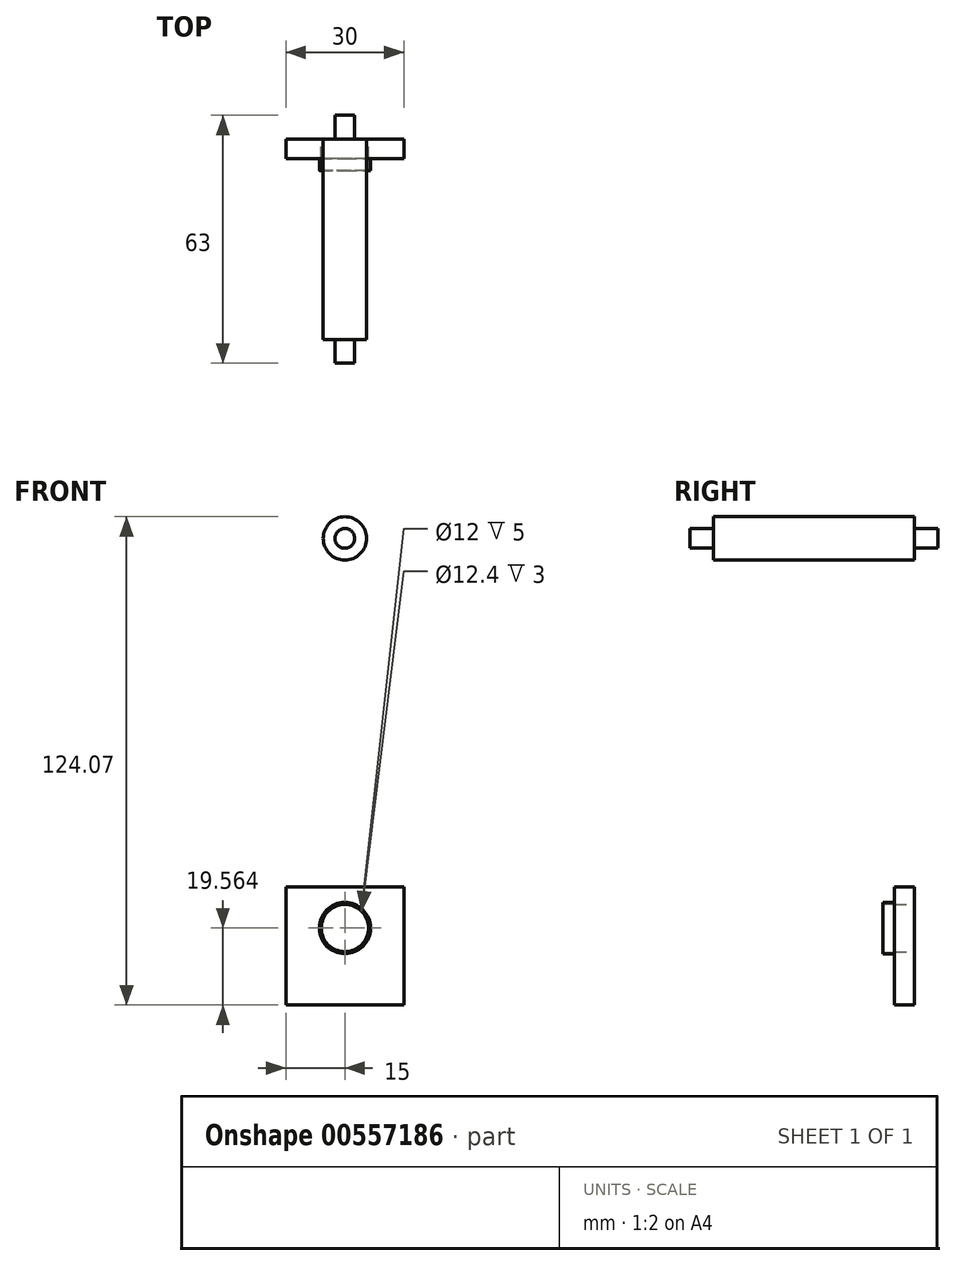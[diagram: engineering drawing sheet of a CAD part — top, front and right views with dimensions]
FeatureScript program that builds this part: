
annotation { "Feature Type Name" : "Feature", "Feature Type Description" : "" }
export const myFeature = defineFeature(function(context is Context, id is Id, definition is map)
    precondition{}
    {
        {
            var Q0;
            Q0=qCreatedBy(makeId("Front.planeOp"),FACE);
            var sketch = newSketch(context, id + "F0", { "sketchPlane" : qUnion([Q0])});
            skCircle(sketch, "E0", {"center": v(0, 0) * mm, "radius": 6 * mm});
            skCircle(sketch, "E1", {"center": v(0, 0) * mm, "radius": 5.7 * mm});
            skSolve(sketch);
        }
        {
            var Q0;
            Q0=makeQuery(id+"F0.imprint","IMPRINT",FACE,{"disambiguationData":[TD([[makeQuery(id+"F0.imprint","IMPRINT",EDGE,{"derivedFrom":sQuery(id+"F0.wireOp",EDGE,"E0")}),1.0]])]});
            extrude(context, id + "F1", {"entities" : qUnion([Q0]), "depth" : 50 * mm, "offsetDistance" : 25 * mm});
        }
        {
            var Q0;
            Q0=qCreatedBy(makeId("Front.planeOp"),FACE);
            var sketch = newSketch(context, id + "F2", { "sketchPlane" : qUnion([Q0])});
            skCircle(sketch, "E2", {"center": v(0, 53.13) * mm, "radius": 5.5 * mm});
            skSolve(sketch);
        }
        {
            var Q0;
            Q0=makeQuery(id+"F2.imprint","IMPRINT",FACE,{"disambiguationData":[TD([[makeQuery(id+"F2.imprint","IMPRINT",EDGE,{"derivedFrom":sQuery(id+"F2.wireOp",EDGE,"E2")}),1.0]])]});
            extrude(context, id + "F3", {"entities" : qUnion([Q0]), "depth" : 51 * mm, "offsetDistance" : 25 * mm});
        }
        {
            var Q0;
            Q0=qCreatedBy(makeId("Front.planeOp"),FACE);
            var sketch = newSketch(context, id + "F4", { "sketchPlane" : qUnion([Q0])});
            skCircle(sketch, "E3", {"center": v(0, 21.61) * mm, "radius": 8.5 * mm});
            skSolve(sketch);
        }
        {
            var Q0;
            Q0=makeQuery(id+"F4.imprint","IMPRINT",FACE,{"disambiguationData":[TD([[makeQuery(id+"F4.imprint","IMPRINT",EDGE,{"derivedFrom":sQuery(id+"F4.wireOp",EDGE,"E3")}),1.0]])]});
            extrude(context, id + "F5", {"entities" : qUnion([Q0]), "depth" : 4 * mm, "offsetDistance" : 25 * mm});
        }
        {
            var Q0;
            Q0=makeQuery(id+"F3.opExtrude","CAP_FACE",FACE,{"disambiguationData":[OSD([sQuery(id+"F2.wireOp",EDGE,"E2")])],"isStart":false});
            var sketch = newSketch(context, id + "F6", { "sketchPlane" : qUnion([Q0])});
            skCircle(sketch, "E4", {"center": v(0, 53.13) * mm, "radius": 2.5 * mm});
            skSolve(sketch);
        }
        {
            var Q0;
            Q0=makeQuery(id+"F6.imprint","IMPRINT",FACE,{"disambiguationData":[TD([[makeQuery(id+"F6.imprint","IMPRINT",EDGE,{"derivedFrom":sQuery(id+"F6.wireOp",EDGE,"E4")}),1.0]])]});
            extrude(context, id + "F7", {"entities" : qUnion([Q0]), "operationType" : NewBodyOperationType.ADD, "depth" : 6 * mm, "offsetDistance" : 25 * mm});
        }
        {
            var Q0;
            Q0=makeQuery(id+"F3.opExtrude","CAP_FACE",FACE,{"disambiguationData":[OSD([sQuery(id+"F2.wireOp",EDGE,"E2")])],"isStart":true});
            var sketch = newSketch(context, id + "F8", { "sketchPlane" : qUnion([Q0])});
            skCircle(sketch, "E5", {"center": v(0, 53.13) * mm, "radius": 2.5 * mm});
            skSolve(sketch);
        }
        {
            var Q0;
            Q0=qCreatedBy(makeId("Front.planeOp"),FACE);
            var sketch = newSketch(context, id + "F9", { "sketchPlane" : qUnion([Q0])});
            skLineSegment(sketch, "E6.bottom", {"start": v(15, -35.44) * mm, "end": v(-15, -35.44) * mm});
            skLineSegment(sketch, "E6.top", {"start": v(15, -65.44) * mm, "end": v(-15, -65.44) * mm});
            skLineSegment(sketch, "E6.left", {"start": v(15, -35.44) * mm, "end": v(15, -65.44) * mm});
            skLineSegment(sketch, "E6.right", {"start": v(-15, -35.44) * mm, "end": v(-15, -65.44) * mm});
            skPoint(sketch, "E6.middle", {"position": v(0, -50.44) * mm});
            skSolve(sketch);
        }
        {
            var Q0;
            Q0=makeQuery(id+"F9.imprint","IMPRINT",FACE,{"disambiguationData":[TD([[makeQuery(id+"F9.imprint","IMPRINT",EDGE,{"derivedFrom":sQuery(id+"F9.wireOp",EDGE,"E6.bottom")}),1.0]])]});
            extrude(context, id + "F10", {"entities" : qUnion([Q0]), "depth" : 5 * mm, "offsetDistance" : 25 * mm});
        }
        {
            var Q0;
            Q0=qCreatedBy(makeId("Front.planeOp"),FACE);
            var sketch = newSketch(context, id + "F11", { "sketchPlane" : qUnion([Q0])});
            skCircle(sketch, "E7", {"center": v(0, -45.88) * mm, "radius": 6 * mm});
            skSolve(sketch);
        }
        {
            var Q0;
            Q0=sQuery(id+"F11.wireOp",VERTEX,"E7.center");
            var Q1;
            Q1=makeQuery(id+"F10.opExtrude","SWEPT_BODY",BODY,{"disambiguationData":[OSD([sQuery(id+"F9.wireOp",EDGE,"E6.bottom"),sQuery(id+"F9.wireOp",EDGE,"E6.top"),sQuery(id+"F9.wireOp",EDGE,"E6.left"),sQuery(id+"F9.wireOp",EDGE,"E6.right")])]});
            hole(context, id + "F12", {"style" : HoleStyle.SIMPLE, "endStyle" : HoleEndStyle.THROUGH, "oppositeDirection" : true, "holeDiameter" : 12 * mm, "majorDiameter" : 5 * mm, "isTappedThrough" : true, "tappedDepth" : 12 * mm, "tapClearance" : 3, "locations" : qUnion([Q0]), "scope" : qUnion([Q1])});
        }
        {
            var Q0;
            Q0=makeQuery(id+"F10.opExtrude","CAP_FACE",FACE,{"disambiguationData":[OSD([sQuery(id+"F9.wireOp",EDGE,"E6.bottom"),sQuery(id+"F9.wireOp",EDGE,"E6.top"),sQuery(id+"F9.wireOp",EDGE,"E6.left"),sQuery(id+"F9.wireOp",EDGE,"E6.right")])],"isStart":false});
            var sketch = newSketch(context, id + "F13", { "sketchPlane" : qUnion([Q0])});
            skCircle(sketch, "E8", {"center": v(0, -45.88) * mm, "radius": 6.2 * mm});
            skCircle(sketch, "E9", {"center": v(0, -45.88) * mm, "radius": 6.5 * mm});
            skSolve(sketch);
        }
        {
            var Q0;
            Q0=makeQuery(id+"F13.imprint","IMPRINT",FACE,{"disambiguationData":[TD([[makeQuery(id+"F13.imprint","IMPRINT",EDGE,{"derivedFrom":sQuery(id+"F13.wireOp",EDGE,"E8")}),-1.0]])]});
            extrude(context, id + "F14", {"entities" : qUnion([Q0]), "operationType" : NewBodyOperationType.ADD, "depth" : 3 * mm, "offsetDistance" : 25 * mm});
        }
        {
            var Q0;
            Q0=makeQuery(id+"F5.opExtrude","CAP_FACE",FACE,{"disambiguationData":[OSD([sQuery(id+"F4.wireOp",EDGE,"E3")])],"isStart":false});
            var sketch = newSketch(context, id + "F15", { "sketchPlane" : qUnion([Q0])});
            skCircle(sketch, "E10", {"center": v(0, 21.61) * mm, "radius": 5.5 * mm});
            skSolve(sketch);
        }
        {
            var Q0;
            Q0=makeQuery(id+"F15.imprint","IMPRINT",FACE,{"disambiguationData":[TD([[makeQuery(id+"F15.imprint","IMPRINT",EDGE,{"derivedFrom":sQuery(id+"F15.wireOp",EDGE,"E10")}),1.0]])]});
            extrude(context, id + "F16", {"entities" : qUnion([Q0]), "operationType" : NewBodyOperationType.ADD, "depth" : 39 * mm, "offsetDistance" : 25 * mm});
        }
        {
            var Q0;
            Q0=makeQuery(id+"F16.opExtrude","CAP_FACE",FACE,{"disambiguationData":[OSD([sQuery(id+"F15.wireOp",EDGE,"E10")])],"isStart":false});
            var sketch = newSketch(context, id + "F17", { "sketchPlane" : qUnion([Q0])});
            skCircle(sketch, "E11", {"center": v(0, 21.61) * mm, "radius": 2.5 * mm});
            skSolve(sketch);
        }
        {
            var Q0;
            Q0=sQuery(id+"F17.wireOp",VERTEX,"E11.center");
            var Q1;
            Q1=makeQuery(id+"F5.opExtrude","SWEPT_BODY",BODY,{"disambiguationData":[OSD([sQuery(id+"F4.wireOp",EDGE,"E3")])]});
            hole(context, id + "F18", {"style" : HoleStyle.SIMPLE, "endStyle" : HoleEndStyle.BLIND, "holeDiameter" : 5 * mm, "majorDiameter" : 5 * mm, "holeDepth" : 8 * mm, "isTappedThrough" : true, "tappedDepth" : 12 * mm, "tapClearance" : 3, "locations" : qUnion([Q0]), "scope" : qUnion([Q1])});
        }
        {
            var Q0;
            Q0=makeQuery(id+"F8.imprint","IMPRINT",FACE,{"disambiguationData":[TD([[makeQuery(id+"F8.imprint","IMPRINT",EDGE,{"derivedFrom":sQuery(id+"F8.wireOp",EDGE,"E5")}),1.0]])]});
            extrude(context, id + "F19", {"entities" : qUnion([Q0]), "operationType" : NewBodyOperationType.ADD, "depth" : 6 * mm, "offsetDistance" : 25 * mm});
        }
        {
            var Q0;
            Q0=makeQuery(id+"F1.opExtrude","SWEPT_BODY",BODY,{"disambiguationData":[OSD([sQuery(id+"F0.wireOp",EDGE,"E0"),sQuery(id+"F0.wireOp",EDGE,"E1")])]});
            deleteBodies(context, id + "F20", {"entities" : qUnion([Q0])});
        }
        {
            var Q0;
            Q0=makeQuery(id+"F5.opExtrude","SWEPT_BODY",BODY,{"disambiguationData":[OSD([sQuery(id+"F4.wireOp",EDGE,"E3")])]});
            deleteBodies(context, id + "F21", {"entities" : qUnion([Q0])});
        }
        {
            var Q0;
            Q0=makeQuery(id+"F3.opExtrude","SWEPT_BODY",BODY,{"disambiguationData":[OSD([sQuery(id+"F2.wireOp",EDGE,"E2")])]});
            transform(context, id + "F22", {"entities" : qUnion([Q0]), "transformType" : TransformType.TRANSLATION_3D, "dx" : 0 * mm, "dy" : 0 * mm, "dz" : 0 * mm, "makeCopy" : true});
        }
        {
            var Q0;
            Q0=makeQuery(id+"F22.opPattern","COPY",BODY,{"derivedFrom":makeQuery(id+"F3.opExtrude","SWEPT_BODY",BODY,{"disambiguationData":[OSD([sQuery(id+"F2.wireOp",EDGE,"E2")])]}),"instanceName":"1"});
            deleteBodies(context, id + "F23", {"entities" : qUnion([Q0])});
        }
    });
